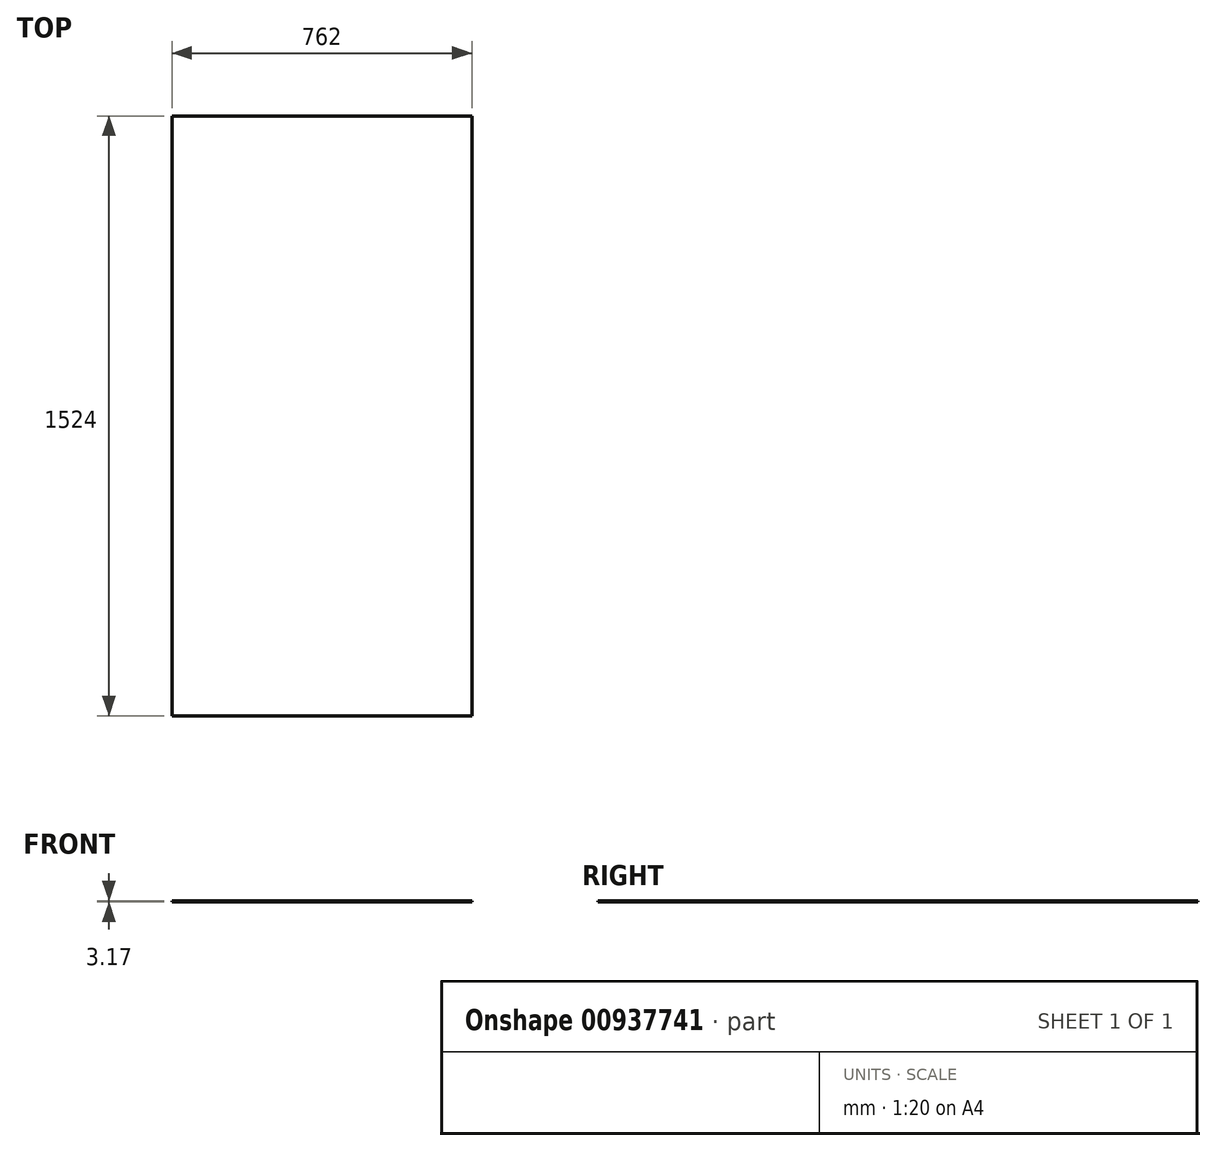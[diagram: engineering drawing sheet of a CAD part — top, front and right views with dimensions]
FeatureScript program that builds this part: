
annotation { "Feature Type Name" : "Feature", "Feature Type Description" : "" }
export const myFeature = defineFeature(function(context is Context, id is Id, definition is map)
    precondition{}
    {
        {
            var Q0;
            Q0=qCreatedBy(makeId("Top.planeOp"),FACE);
            var sketch = newSketch(context, id + "F0", { "sketchPlane" : qUnion([Q0])});
            skLineSegment(sketch, "E0.bottom", {"start": v(381, 762) * mm, "end": v(-381, 762) * mm});
            skLineSegment(sketch, "E0.top", {"start": v(381, -762) * mm, "end": v(-381, -762) * mm});
            skLineSegment(sketch, "E0.left", {"start": v(381, 762) * mm, "end": v(381, -762) * mm});
            skLineSegment(sketch, "E0.right", {"start": v(-381, 762) * mm, "end": v(-381, -762) * mm});
            skPoint(sketch, "E0.middle", {"position": v(0, 0) * mm});
            skSolve(sketch);
        }
        {
            var Q0;
            Q0=makeQuery(id+"F0.imprint","IMPRINT",FACE,{"disambiguationData":[TD([[makeQuery(id+"F0.imprint","IMPRINT",EDGE,{"derivedFrom":sQuery(id+"F0.wireOp",EDGE,"E0.bottom")}),1.0]])]});
            extrude(context, id + "F1", {"entities" : qUnion([Q0]), "depth" : 3.17 * mm, "offsetDistance" : 25.4 * mm});
        }
    });
